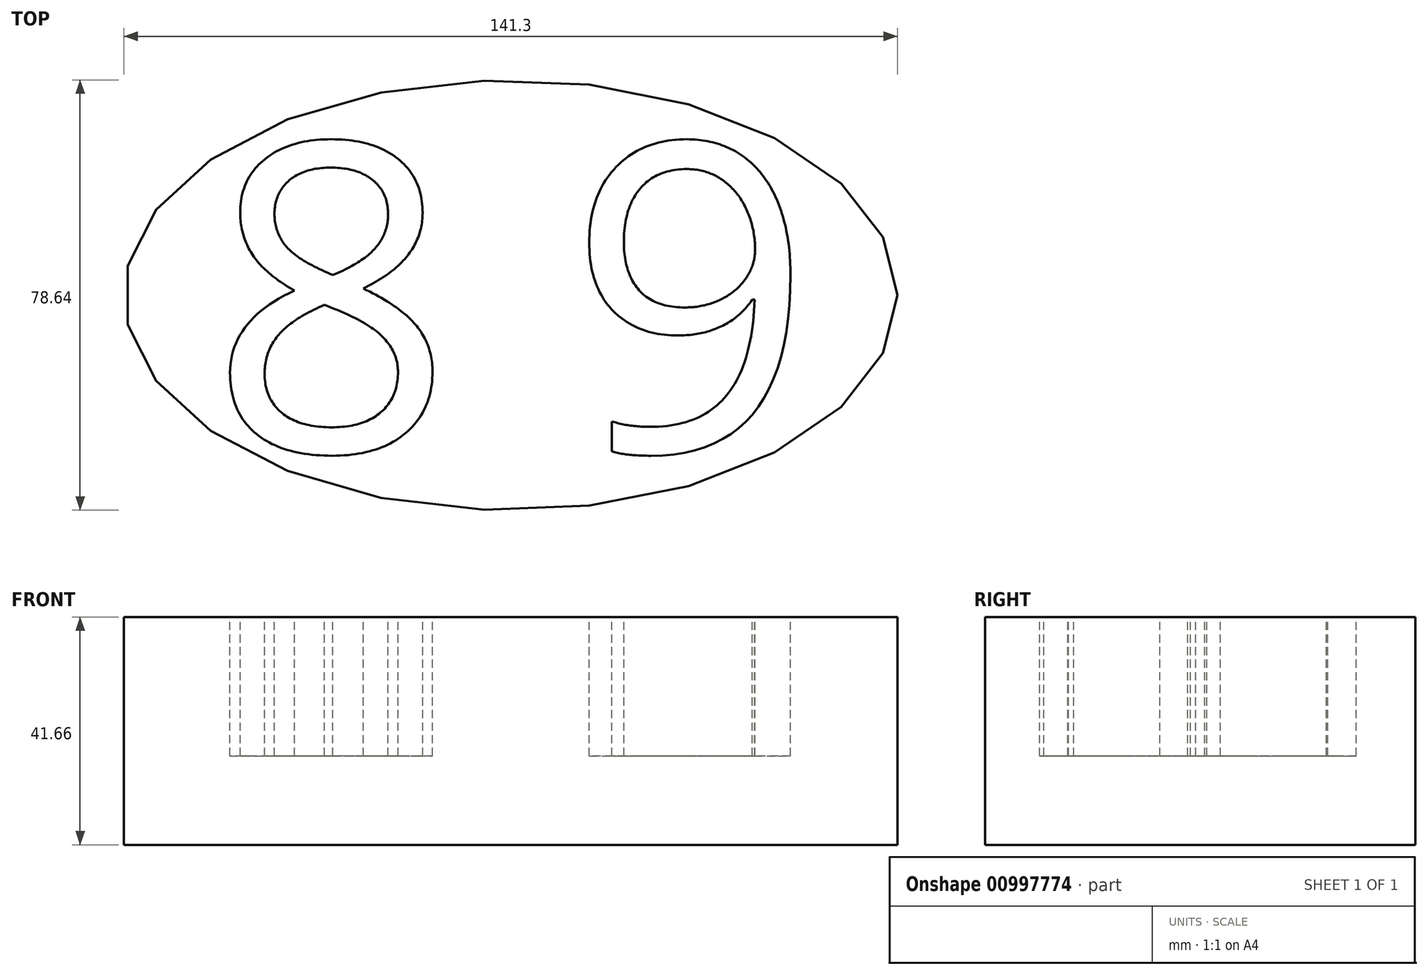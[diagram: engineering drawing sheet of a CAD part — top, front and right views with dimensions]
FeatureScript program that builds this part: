
annotation { "Feature Type Name" : "Feature", "Feature Type Description" : "" }
export const myFeature = defineFeature(function(context is Context, id is Id, definition is map)
    precondition{}
    {
        {
            var Q0;
            Q0=qCreatedBy(makeId("Top.planeOp"),FACE);
            var sketch = newSketch(context, id + "F0", { "sketchPlane" : qUnion([Q0])});
            skEllipse(sketch, "E0", {"center": v(0, 0) * mm, "majorRadius": 70.65 * mm, "minorRadius": 39.32 * mm, "majorAxis": v(1, 0)});
            skSolve(sketch);
        }
        {
            var Q0;
            Q0=makeQuery(id+"F0.imprint","IMPRINT",FACE,{"disambiguationData":[TD([[makeQuery(id+"F0.imprint","IMPRINT",EDGE,{"derivedFrom":sQuery(id+"F0.wireOp",EDGE,"E0")}),1.0]])]});
            extrude(context, id + "F1", {"entities" : qUnion([Q0]), "depth" : 41.66 * mm, "offsetDistance" : 25.4 * mm});
        }
        {
            var Q0;
            Q0=makeQuery(id+"F1.opExtrude","CAP_FACE",FACE,{"disambiguationData":[OSD([sQuery(id+"F0.wireOp",EDGE,"E0")])],"isStart":false});
            var sketch = newSketch(context, id + "F2", { "sketchPlane" : qUnion([Q0])});
            skText(sketch, "E1", { "text": "8 9", "fontName": "OpenSans-Regular.ttf"});
            const initialGuessF2  = {"E1": [-0.05528, -0.02858, 1, 0, 0.05676]};
            skSetInitialGuess(sketch, initialGuessF2);
            skSolve(sketch);
        }
        {
            var Q0;
            Q0 = qSketchRegion(id + "F2", true);
            extrude(context, id + "F3", {"entities" : qUnion([Q0]), "operationType" : NewBodyOperationType.REMOVE, "oppositeDirection" : true, "depth" : 25.4 * mm, "offsetDistance" : 25.4 * mm});
        }
    });
